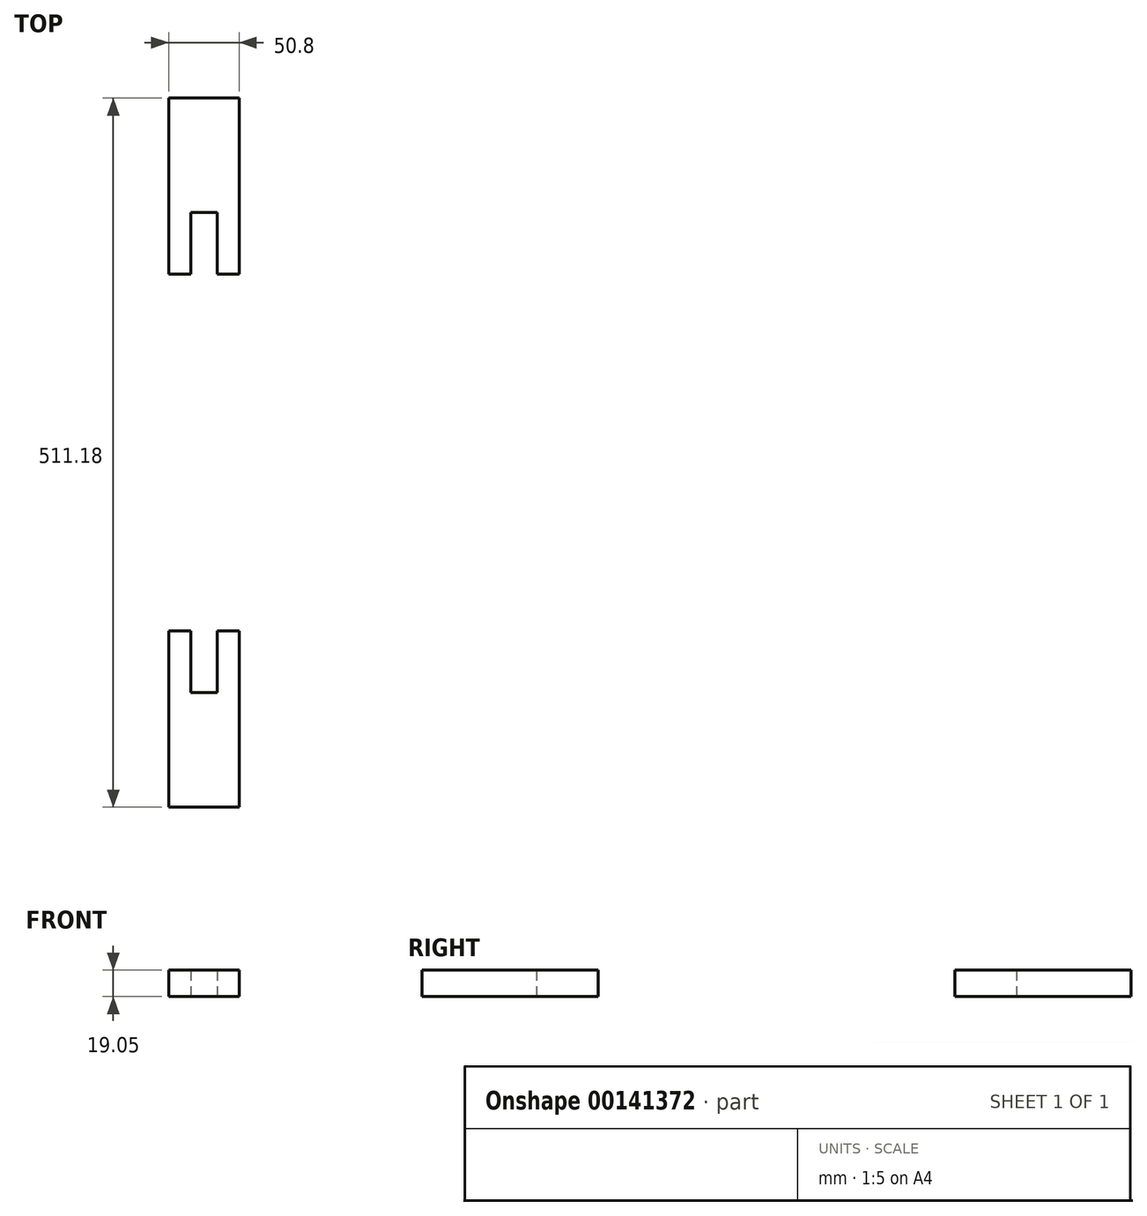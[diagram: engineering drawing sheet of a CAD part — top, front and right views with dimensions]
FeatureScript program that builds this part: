
annotation { "Feature Type Name" : "Feature", "Feature Type Description" : "" }
export const myFeature = defineFeature(function(context is Context, id is Id, definition is map)
    precondition{}
    {
        {
            var Q0;
            Q0=qCreatedBy(makeId("Top.planeOp"),FACE);
            var sketch = newSketch(context, id + "F0", { "sketchPlane" : qUnion([Q0])});
            skLineSegment(sketch, "E0.top", {"start": v(-25.4, -84.14) * mm, "end": v(25.4, -84.14) * mm});
            skLineSegment(sketch, "E0.left", {"start": v(-25.4, 42.86) * mm, "end": v(-25.4, -84.14) * mm});
            skLineSegment(sketch, "E0.right", {"start": v(25.4, 42.86) * mm, "end": v(25.4, -84.14) * mm});
            skLineSegment(sketch, "E1", {"start": v(-25.4, 42.86) * mm, "end": v(-9.53, 42.86) * mm});
            skLineSegment(sketch, "E2", {"start": v(9.53, 42.86) * mm, "end": v(25.4, 42.86) * mm});
            skLineSegment(sketch, "E3", {"start": v(-9.53, 42.86) * mm, "end": v(-9.52, -1.59) * mm});
            skLineSegment(sketch, "E4", {"start": v(-9.52, -1.59) * mm, "end": v(9.53, -1.59) * mm});
            skLineSegment(sketch, "E5", {"start": v(9.53, -1.59) * mm, "end": v(9.53, 42.86) * mm});
            skLineSegment(sketch, "E6", {"start": v(-102.45, 171.45) * mm, "end": v(107.44, 171.45) * mm});
            skLineSegment(sketch, "E7.MirrorCS", {"start": v(25.4, 300.04) * mm, "end": v(25.4, 427.04) * mm});
            skLineSegment(sketch, "E8.MirrorCS", {"start": v(-25.4, 300.04) * mm, "end": v(-9.53, 300.04) * mm});
            skLineSegment(sketch, "E9.MirrorCS", {"start": v(-9.52, 344.49) * mm, "end": v(9.53, 344.49) * mm});
            skLineSegment(sketch, "E10.MirrorCS", {"start": v(9.53, 344.49) * mm, "end": v(9.53, 300.04) * mm});
            skLineSegment(sketch, "E11.MirrorCS", {"start": v(-25.4, 300.04) * mm, "end": v(-25.4, 427.04) * mm});
            skLineSegment(sketch, "E12.MirrorCS", {"start": v(9.53, 300.04) * mm, "end": v(25.4, 300.04) * mm});
            skLineSegment(sketch, "E13.MirrorCS", {"start": v(-25.4, 427.04) * mm, "end": v(25.4, 427.04) * mm});
            skLineSegment(sketch, "E14.MirrorCS", {"start": v(-9.53, 300.04) * mm, "end": v(-9.52, 344.49) * mm});
            skSolve(sketch);
        }
        {
            var Q0;
            Q0=makeQuery(id+"F0.imprint","IMPRINT",FACE,{"disambiguationData":[TD([[makeQuery(id+"F0.imprint","IMPRINT",EDGE,{"derivedFrom":sQuery(id+"F0.wireOp",EDGE,"E0.top")}),1.0]])]});
            var Q1;
            Q1=makeQuery(id+"F0.imprint","IMPRINT",FACE,{"disambiguationData":[TD([[makeQuery(id+"F0.imprint","IMPRINT",EDGE,{"derivedFrom":sQuery(id+"F0.wireOp",EDGE,"E7.MirrorCS")}),1.0]])]});
            extrude(context, id + "F1", {"entities" : qUnion([Q0, Q1]), "depth" : 19.05 * mm});
        }
    });
